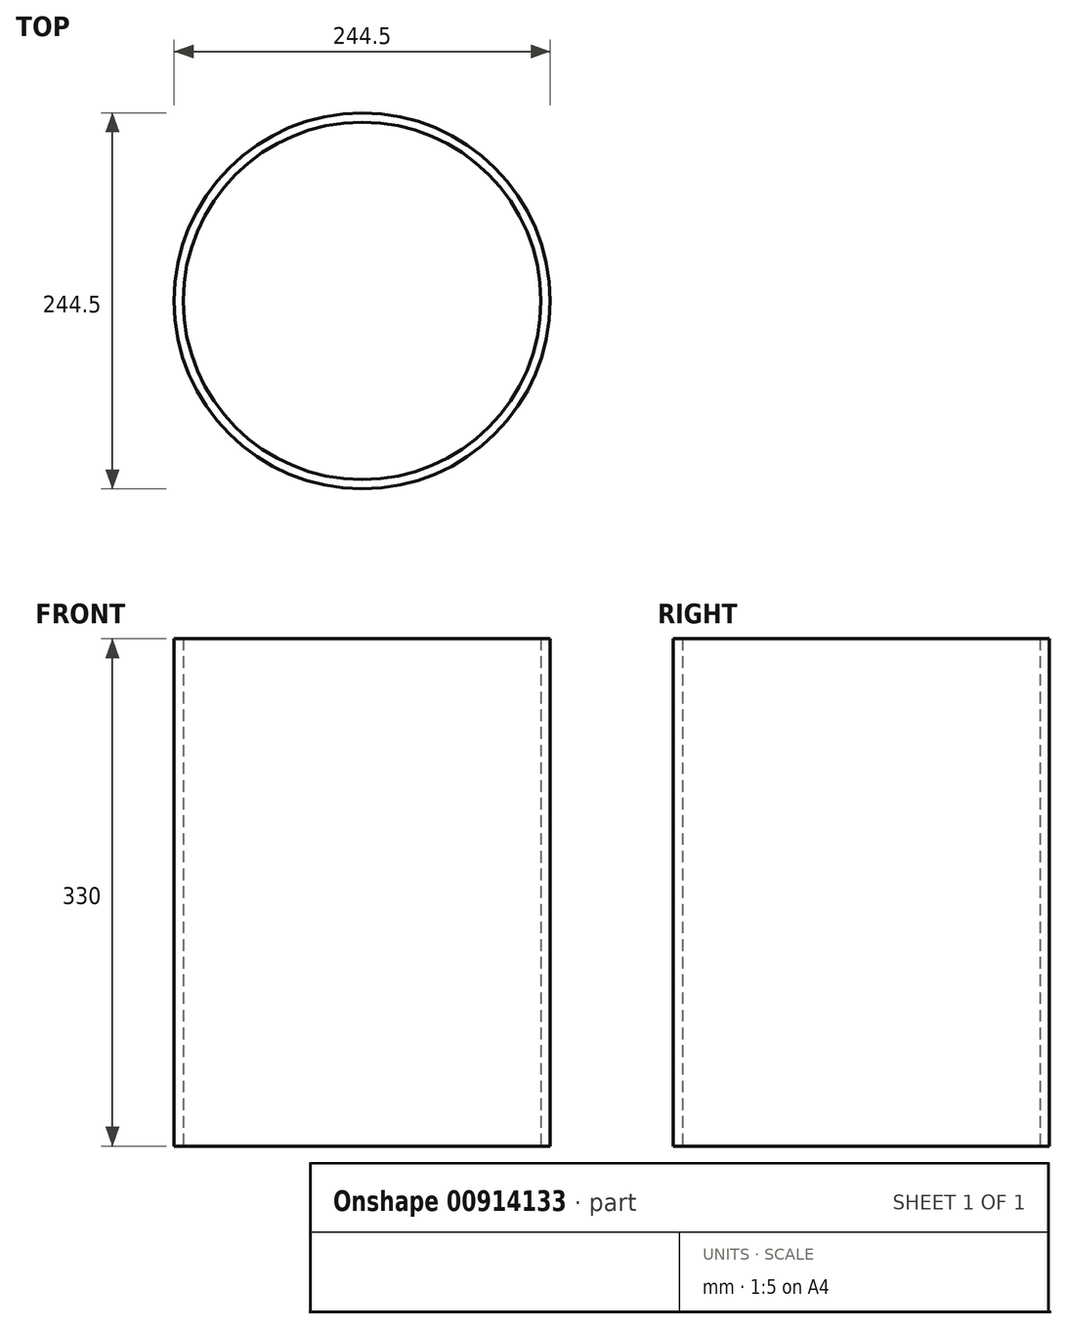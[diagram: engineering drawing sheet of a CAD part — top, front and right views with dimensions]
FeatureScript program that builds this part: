
annotation { "Feature Type Name" : "Feature", "Feature Type Description" : "" }
export const myFeature = defineFeature(function(context is Context, id is Id, definition is map)
    precondition{}
    {
        {
            var Q0;
            Q0=qCreatedBy(makeId("Top.planeOp"),FACE);
            var sketch = newSketch(context, id + "F0", { "sketchPlane" : qUnion([Q0])});
            skCircle(sketch, "E0", {"center": v(0, 0) * mm, "radius": 116.25 * mm});
            skCircle(sketch, "E1.0", {"center": v(0, 0) * mm, "radius": 122.25 * mm});
            skSolve(sketch);
        }
        {
            var Q0;
            Q0=makeQuery(id+"F0.imprint","IMPRINT",FACE,{"disambiguationData":[TD([[makeQuery(id+"F0.imprint","IMPRINT",EDGE,{"derivedFrom":sQuery(id+"F0.wireOp",EDGE,"E0")}),-1.0]])]});
            extrude(context, id + "F1", {"entities" : qUnion([Q0]), "depth" : 330 * mm, "offsetDistance" : 25 * mm});
        }
    });
